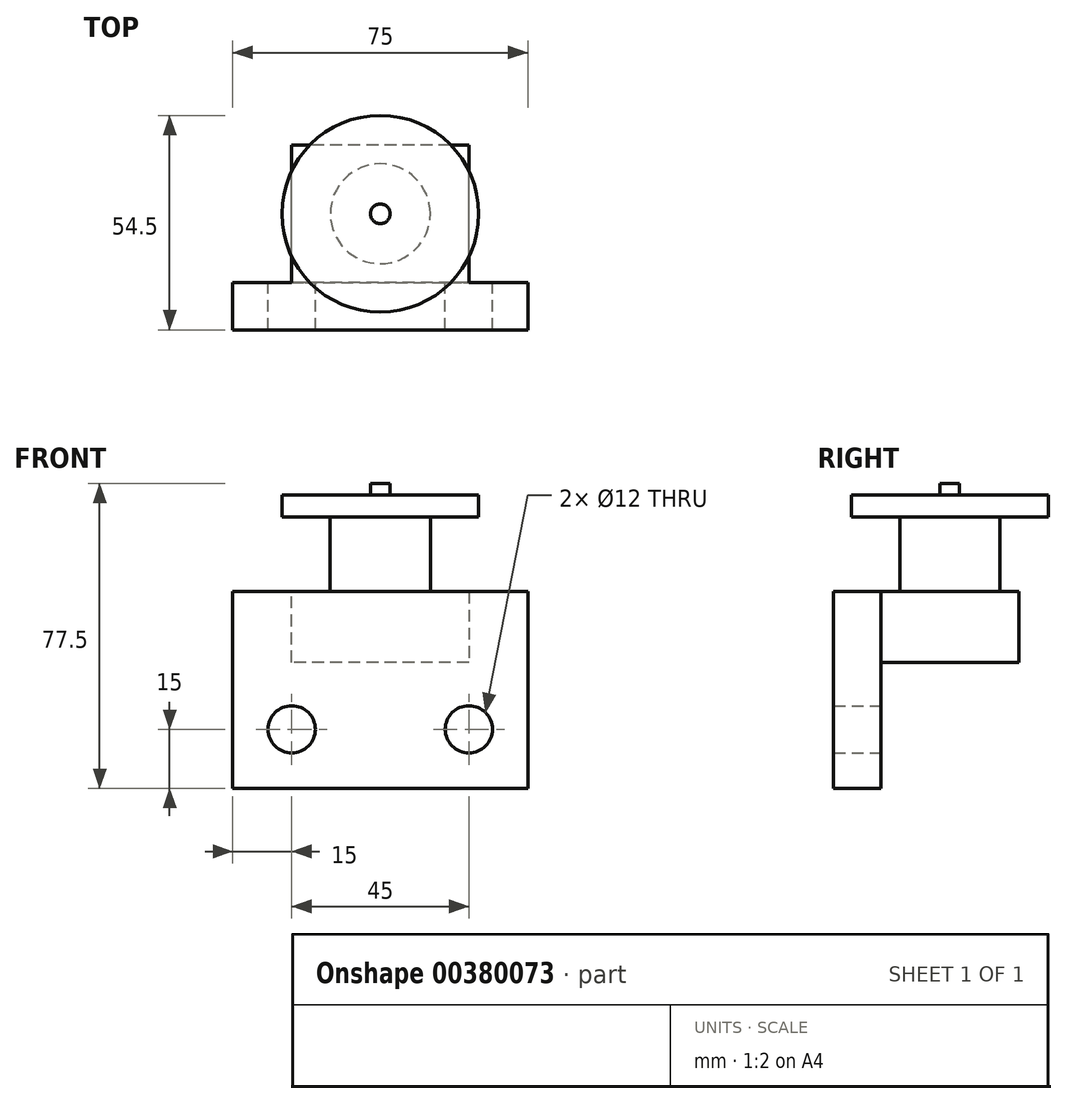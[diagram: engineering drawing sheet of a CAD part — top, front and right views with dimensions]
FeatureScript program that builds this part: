
annotation { "Feature Type Name" : "Feature", "Feature Type Description" : "" }
export const myFeature = defineFeature(function(context is Context, id is Id, definition is map)
    precondition{}
    {
        {
            var Q0;
            Q0=qCreatedBy(makeId("Top.planeOp"),FACE);
            var sketch = newSketch(context, id + "F0", { "sketchPlane" : qUnion([Q0])});
            skLineSegment(sketch, "E0.bottom", {"start": v(50, -17.5) * mm, "end": v(-50, -17.5) * mm});
            skLineSegment(sketch, "E0.top", {"start": v(50, 17.5) * mm, "end": v(-50, 17.5) * mm});
            skLineSegment(sketch, "E0.left", {"start": v(50, -17.5) * mm, "end": v(50, 17.5) * mm});
            skLineSegment(sketch, "E0.right", {"start": v(-50, -17.5) * mm, "end": v(-50, 17.5) * mm});
            skPoint(sketch, "E0.middle", {"position": v(0, 0) * mm});
            skSolve(sketch);
        }
        {
            var Q0;
            Q0=makeQuery(id+"F0.imprint","IMPRINT",FACE,{"disambiguationData":[TD([[makeQuery(id+"F0.imprint","IMPRINT",EDGE,{"derivedFrom":sQuery(id+"F0.wireOp",EDGE,"E0.bottom")}),-1.0]])]});
            extrude(context, id + "F1", {"entities" : qUnion([Q0]), "depth" : -18 * mm});
        }
        {
            var Q0;
            Q0=makeQuery(id+"F1.opExtrude","CAP_FACE",FACE,{"disambiguationData":[OSD([sQuery(id+"F0.wireOp",EDGE,"E0.bottom"),sQuery(id+"F0.wireOp",EDGE,"E0.top"),sQuery(id+"F0.wireOp",EDGE,"E0.left"),sQuery(id+"F0.wireOp",EDGE,"E0.right")])],"isStart":true});
            var sketch = newSketch(context, id + "F2", { "sketchPlane" : qUnion([Q0])});
            skCircle(sketch, "E1", {"center": v(0, 0) * mm, "radius": 12.7 * mm});
            skSolve(sketch);
        }
        {
            var Q0;
            Q0=makeQuery(id+"F2.imprint","IMPRINT",FACE,{"disambiguationData":[TD([[makeQuery(id+"F2.imprint","IMPRINT",EDGE,{"derivedFrom":sQuery(id+"F2.wireOp",EDGE,"E1")}),1.0]])]});
            extrude(context, id + "F3", {"entities" : qUnion([Q0]), "operationType" : NewBodyOperationType.ADD, "depth" : 19 * mm});
        }
        {
            var Q0;
            Q0=makeQuery(id+"F3.opExtrude","CAP_FACE",FACE,{"disambiguationData":[OSD([sQuery(id+"F2.wireOp",EDGE,"E1")])],"isStart":false});
            var sketch = newSketch(context, id + "F4", { "sketchPlane" : qUnion([Q0])});
            skCircle(sketch, "E2", {"center": v(0, 0) * mm, "radius": 25 * mm});
            skSolve(sketch);
        }
        {
            var Q0;
            Q0=makeQuery(id+"F4.imprint","IMPRINT",FACE,{"disambiguationData":[TD([[makeQuery(id+"F4.imprint","IMPRINT",EDGE,{"derivedFrom":sQuery(id+"F4.wireOp",EDGE,"E2")}),1.0]])]});
            var Q1;
            Q1=makeQuery(id+"F4.imprint","IMPRINT",FACE,{"disambiguationData":[TD([[makeQuery(id+"F4.imprint","IMPRINT",EDGE,{"derivedFrom":makeQuery(id+"F3.opExtrude","CAP_EDGE",EDGE,{"disambiguationData":[OSD([sQuery(id+"F2.wireOp",EDGE,"E1")])],"isStart":false})}),1.0]])]});
            extrude(context, id + "F5", {"entities" : qUnion([Q0, Q1]), "operationType" : NewBodyOperationType.ADD, "depth" : 5.5 * mm});
        }
        {
            var Q0;
            Q0=makeQuery(id+"F5.opExtrude","CAP_FACE",FACE,{"disambiguationData":[OSD([sQuery(id+"F4.wireOp",EDGE,"E2")])],"isStart":false});
            var sketch = newSketch(context, id + "F6", { "sketchPlane" : qUnion([Q0])});
            skCircle(sketch, "E3", {"center": v(0, 0) * mm, "radius": 2.5 * mm});
            skSolve(sketch);
        }
        {
            var Q0;
            Q0=qSketchRegion(id+"F6",true);
            extrude(context, id + "F7", {"entities" : qUnion([Q0]), "operationType" : NewBodyOperationType.ADD, "depth" : 3 * mm});
        }
        {
            var Q0;
            Q0=makeQuery(id+"F1.opExtrude","SWEPT_FACE",FACE,{"disambiguationData":[OSD([sQuery(id+"F0.wireOp",EDGE,"E0.bottom")])]});
            var sketch = newSketch(context, id + "F8", { "sketchPlane" : qUnion([Q0])});
            skLineSegment(sketch, "E4.bottom", {"start": v(-50, 0) * mm, "end": v(50, 0) * mm});
            skLineSegment(sketch, "E4.top", {"start": v(-50, -75) * mm, "end": v(50, -75) * mm});
            skLineSegment(sketch, "E4.left", {"start": v(-50, 0) * mm, "end": v(-50, -75) * mm});
            skLineSegment(sketch, "E4.right", {"start": v(50, 0) * mm, "end": v(50, -75) * mm});
            skSolve(sketch);
        }
        {
            var Q0;
            {var subQ0=sQuery(id+"F8.wireOp",EDGE,"E4.top");Q0=makeQuery(id+"F8.imprint","IMPRINT",FACE,{"disambiguationData":[TD([[makeQuery(id+"F8.imprint","IMPRINT",EDGE,{"derivedFrom":subQ0}),1.0]])]});}
            var Q1;
            {var subQ0=sQuery(id+"F8.wireOp",EDGE,"E4.bottom");Q1=makeQuery(id+"F8.imprint","IMPRINT",FACE,{"disambiguationData":[TD([[makeQuery(id+"F8.imprint","IMPRINT",EDGE,{"derivedFrom":subQ0}),1.0]])]});}
            extrude(context, id + "F9", {"entities" : qUnion([Q0, Q1]), "operationType" : NewBodyOperationType.ADD, "depth" : 12 * mm});
        }
        {
            var Q0;
            Q0=makeQuery(id+"F9.opExtrude","CAP_FACE",FACE,{"disambiguationData":[OSD([sQuery(id+"F8.wireOp",EDGE,"E4.bottom"),sQuery(id+"F8.wireOp",EDGE,"E4.top"),sQuery(id+"F8.wireOp",EDGE,"E4.left"),sQuery(id+"F8.wireOp",EDGE,"E4.right")])],"isStart":false});
            var sketch = newSketch(context, id + "F10", { "sketchPlane" : qUnion([Q0])});
            skLineSegment(sketch, "E5", {"start": v(0, 0) * mm, "end": v(-37.5, 0) * mm});
            skLineSegment(sketch, "E6", {"start": v(-37.5, 0) * mm, "end": v(-37.5, -50) * mm});
            skLineSegment(sketch, "E7", {"start": v(-37.5, -50) * mm, "end": v(37.5, -50) * mm});
            skLineSegment(sketch, "E8", {"start": v(37.5, -50) * mm, "end": v(37.5, 0) * mm});
            skLineSegment(sketch, "E9", {"start": v(37.5, 0) * mm, "end": v(0, 0) * mm});
            skLineSegment(sketch, "E10", {"start": v(50, 0) * mm, "end": v(50, -75) * mm});
            skLineSegment(sketch, "E11", {"start": v(50, -75) * mm, "end": v(-50, -75) * mm});
            skLineSegment(sketch, "E12", {"start": v(-50, -75) * mm, "end": v(-50, 0) * mm});
            skLineSegment(sketch, "E13", {"start": v(-50, 0) * mm, "end": v(50, 0) * mm});
            skSolve(sketch);
        }
        {
            var Q0;
            {var subQ2=sQuery(id+"F10.wireOp",EDGE,"E6");Q0=makeQuery(id+"F10.imprint","IMPRINT",FACE,{"disambiguationData":[TD([[makeQuery(id+"F10.imprint","IMPRINT",EDGE,{"derivedFrom":subQ2}),-1.0]])]});}
            extrude(context, id + "F11", {"entities" : qUnion([Q0]), "operationType" : NewBodyOperationType.REMOVE, "oppositeDirection" : true, "depth" : 50 * mm});
        }
        {
            var Q0;
            Q0=makeQuery(id+"F9.opExtrude","CAP_FACE",FACE,{"disambiguationData":[OSD([sQuery(id+"F8.wireOp",EDGE,"E4.bottom"),sQuery(id+"F8.wireOp",EDGE,"E4.top"),sQuery(id+"F8.wireOp",EDGE,"E4.left"),sQuery(id+"F8.wireOp",EDGE,"E4.right")])],"isStart":true});
            var sketch = newSketch(context, id + "F12", { "sketchPlane" : qUnion([Q0])});
            skLineSegment(sketch, "E14", {"start": v(37.5, -50) * mm, "end": v(37.5, -35) * mm, "construction": true});
            skLineSegment(sketch, "E15", {"start": v(37.5, -35) * mm, "end": v(22.5, -35) * mm, "construction": true});
            skLineSegment(sketch, "E16", {"start": v(22.5, -35) * mm, "end": v(-22.5, -35) * mm, "construction": true});
            skLineSegment(sketch, "E17", {"start": v(-22.5, -35) * mm, "end": v(-37.5, -35) * mm, "construction": true});
            skSolve(sketch);
        }
        {
            var Q0;
            Q0=sQuery(id+"F12.wireOp",VERTEX,"E17.start");
            var Q1;
            Q1=sQuery(id+"F12.wireOp",VERTEX,"E16.start");
            var Q2;
            Q2=makeQuery(id+"F1.opExtrude","SWEPT_BODY",BODY,{"disambiguationData":[OSD([sQuery(id+"F0.wireOp",EDGE,"E0.bottom"),sQuery(id+"F0.wireOp",EDGE,"E0.top"),sQuery(id+"F0.wireOp",EDGE,"E0.left"),sQuery(id+"F0.wireOp",EDGE,"E0.right")])]});
            hole(context, id + "F13", {"style" : HoleStyle.SIMPLE, "endStyle" : HoleEndStyle.BLIND, "holeDiameter" : 12 * mm, "holeDepth" : 12 * mm, "isTappedThrough" : true, "tappedDepth" : 12 * mm, "tapClearance" : 3, "locations" : qUnion([Q0, Q1]), "scope" : qUnion([Q2])});
        }
        {
            var Q0;
            Q0=makeQuery(id+"F1.opExtrude","SWEPT_FACE",FACE,{"disambiguationData":[OSD([sQuery(id+"F0.wireOp",EDGE,"E0.top")])]});
            var sketch = newSketch(context, id + "F14", { "sketchPlane" : qUnion([Q0])});
            skLineSegment(sketch, "E18.bottom", {"start": v(37.5, -18) * mm, "end": v(22.5, -18) * mm});
            skLineSegment(sketch, "E18.top", {"start": v(37.5, 0) * mm, "end": v(22.5, 0) * mm});
            skLineSegment(sketch, "E18.left", {"start": v(37.5, -18) * mm, "end": v(37.5, 0) * mm});
            skLineSegment(sketch, "E18.right", {"start": v(22.5, -18) * mm, "end": v(22.5, 0) * mm});
            skLineSegment(sketch, "E19.bottom", {"start": v(-37.5, 0) * mm, "end": v(-22.5, 0) * mm});
            skLineSegment(sketch, "E19.top", {"start": v(-37.5, -18) * mm, "end": v(-22.5, -18) * mm});
            skLineSegment(sketch, "E19.left", {"start": v(-37.5, 0) * mm, "end": v(-37.5, -18) * mm});
            skLineSegment(sketch, "E19.right", {"start": v(-22.5, 0) * mm, "end": v(-22.5, -18) * mm});
            skSolve(sketch);
        }
        {
            var Q0;
            Q0=makeQuery(id+"F14.imprint","IMPRINT",FACE,{"disambiguationData":[TD([[makeQuery(id+"F14.imprint","IMPRINT",EDGE,{"derivedFrom":sQuery(id+"F14.wireOp",EDGE,"E19.bottom")}),-1.0]])]});
            var Q1;
            Q1=makeQuery(id+"F14.imprint","IMPRINT",FACE,{"disambiguationData":[TD([[makeQuery(id+"F14.imprint","IMPRINT",EDGE,{"derivedFrom":sQuery(id+"F14.wireOp",EDGE,"E18.bottom")}),1.0]])]});
            extrude(context, id + "F15", {"entities" : qUnion([Q0, Q1]), "operationType" : NewBodyOperationType.REMOVE, "oppositeDirection" : true, "depth" : 35 * mm});
        }
    });
